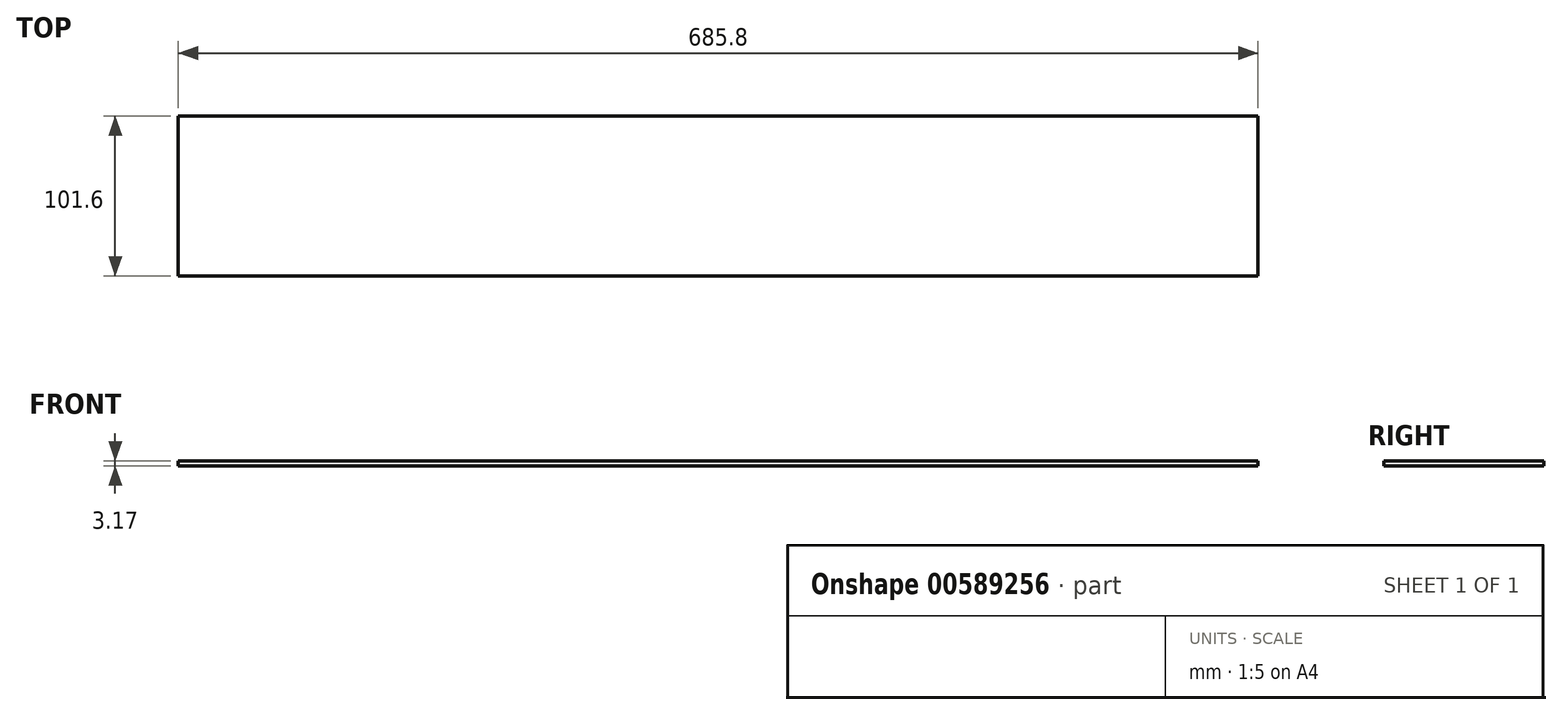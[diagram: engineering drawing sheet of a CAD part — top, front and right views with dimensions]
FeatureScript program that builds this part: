
annotation { "Feature Type Name" : "Feature", "Feature Type Description" : "" }
export const myFeature = defineFeature(function(context is Context, id is Id, definition is map)
    precondition{}
    {
        {
            var Q0;
            Q0=qCreatedBy(makeId("Top.planeOp"),FACE);
            var sketch = newSketch(context, id + "F0", { "sketchPlane" : qUnion([Q0])});
            skLineSegment(sketch, "E0.bottom", {"start": v(342.9, -50.8) * mm, "end": v(-342.9, -50.8) * mm});
            skLineSegment(sketch, "E0.top", {"start": v(342.9, 50.8) * mm, "end": v(-342.9, 50.8) * mm});
            skLineSegment(sketch, "E0.left", {"start": v(342.9, -50.8) * mm, "end": v(342.9, 50.8) * mm});
            skLineSegment(sketch, "E0.right", {"start": v(-342.9, -50.8) * mm, "end": v(-342.9, 50.8) * mm});
            skPoint(sketch, "E0.middle", {"position": v(0, 0) * mm});
            skSolve(sketch);
        }
        {
            var Q0;
            Q0=makeQuery(id+"F0.imprint","IMPRINT",FACE,{"disambiguationData":[TD([[makeQuery(id+"F0.imprint","IMPRINT",EDGE,{"derivedFrom":sQuery(id+"F0.wireOp",EDGE,"E0.bottom")}),-1.0]])]});
            extrude(context, id + "F1", {"entities" : qUnion([Q0]), "depth" : (1 / 8 * 25.4) * mm, "offsetDistance" : 25 * mm});
        }
        {
            var Q0;
            Q0=makeQuery(id+"F1.opExtrude","CAP_FACE",FACE,{"disambiguationData":[OSD([sQuery(id+"F0.wireOp",EDGE,"E0.bottom"),sQuery(id+"F0.wireOp",EDGE,"E0.top"),sQuery(id+"F0.wireOp",EDGE,"E0.left"),sQuery(id+"F0.wireOp",EDGE,"E0.right")])],"isStart":false});
            var sketch = newSketch(context, id + "F2", { "sketchPlane" : qUnion([Q0])});
            skLineSegment(sketch, "E1", {"start": v(88.9, 136.34) * mm, "end": v(88.9, -151.55) * mm, "construction": true});
            skLineSegment(sketch, "E2", {"start": v(65.78, 25.4) * mm, "end": v(115.15, 25.4) * mm, "construction": true});
            skLineSegment(sketch, "E3", {"start": v(66.9, -25.4) * mm, "end": v(121.46, -25.4) * mm, "construction": true});
            skPoint(sketch, "E4", {"position": v(88.9, 25.4) * mm});
            skPoint(sketch, "E5", {"position": v(88.9, -25.4) * mm});
            skSolve(sketch);
        }
        {
            var Q0;
            Q0=makeQuery(id+"F2.imprint","IMPRINT",FACE,{"disambiguationData":[TD([[makeQuery(id+"F2.imprint","IMPRINT",EDGE,{"derivedFrom":makeQuery(id+"F1.opExtrude","CAP_EDGE",EDGE,{"disambiguationData":[OSD([sQuery(id+"F0.wireOp",EDGE,"E0.bottom")])],"isStart":false})}),-1.0]])]});
            var sketch = newSketch(context, id + "F3", { "sketchPlane" : qUnion([Q0])});
            skLineSegment(sketch, "E6", {"start": v(282.35, 0) * mm, "end": v(337.68, 0) * mm, "construction": true});
            skLineSegment(sketch, "E7", {"start": v(310.01, 21.97) * mm, "end": v(310.01, -20.4) * mm, "construction": true});
            skPoint(sketch, "E7.startSnap0", {"position": v(310.01, 0) * mm});
            skSolve(sketch);
        }
    });
